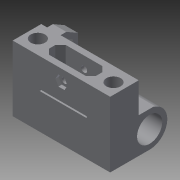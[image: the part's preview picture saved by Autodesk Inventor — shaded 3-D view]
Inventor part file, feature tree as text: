
AUTODESK INVENTOR PART (.ipt)
format: ipt  version: 2015 (Build 190159000, 159)  size: 218,112 bytes
history: native  units: mm
features: sketch x9, extrude x7, hole x3
ambient origin geometry x8: Origin, YZ Plane, XZ Plane, XY Plane, X Axis, Y Axis, Z Axis, Center Point
bodies: Solid1 (feature_tree)
feature tree (19):
  extrude  "Extrusion1"  Depth=39.0mm
  sketch  "Sketch2"  dims[d2=35.0mm d3=0.0mm d5=15.0mm]
  extrude  "Extrusion2"  Depth=15.0mm
  extrude  "Extrusion3"  Depth=8.0mm
  extrude  "Extrusion4"  Depth=3.5mm
  extrude  "Extrusion5"  Depth=17.0mm
  hole  "Hole1"  [1 undecoded]
  hole  "Hole2"  [1 undecoded]
  hole  "Hole3"  [1 undecoded]
  extrude  "Extrusion6"  Depth=10.0mm
  extrude  "Extrusion7"  Depth=28.0mm
  sketch  "Sketch1"  dims[d0=58.0mm d1=39.0mm]
  sketch  "Sketch3"  dims[d6=3.0mm d8=8.0mm]
  sketch  "Sketch4"  dims[d11=17.0mm d12=3.5mm]
  sketch  "Sketch5"  dims[d13=23.5mm d14=17.0mm]
  sketch  "Sketch7"  dims[d15=10.0mm d16=0.0mm d18=8.0mm]
  sketch  "Sketch8"  dims[d19=14.5mm d20=0.0mm d21=1.0mm]
  sketch  "Sketch9"  dims[d22=28.0mm d23=14.0mm]
  sketch  "Sketch10"  dims[d24=14.5mm d25=0.0mm d26=10.0mm d27=28.0mm d28=3.5mm d29=135.0deg d30=135.0deg d31=3.858mm d32=29.0mm d33=14.5mm d34=0.0mm d35=45.0mm d36=8.5mm d37=22.5mm d38=8.5mm d39=6.0mm d40=3.023mm d41=2.0mm d42=14.3117mm d43=37.0mm d44=0.0mm d45=14.0mm d46=7.0mm d47=3.6mm d48=6.0mm d49=6.2mm d50=2.0mm d51=14.3117mm d52=37.0mm d53=0.0mm d54=5.7mm d55=6.0mm d56=6.2mm d57=2.0mm d58=14.3117mm d59=23.5mm d60=0.0mm d63=3.6mm d64=2.0mm d65=0.0mm d66=4.5mm d67=5.0mm d68=0.0mm]
note: 3 required parameter values undecoded (feature->parameter linkage not recoverable at this tier; creation-order binding heuristic only, values carry confidence <= 0.55)
